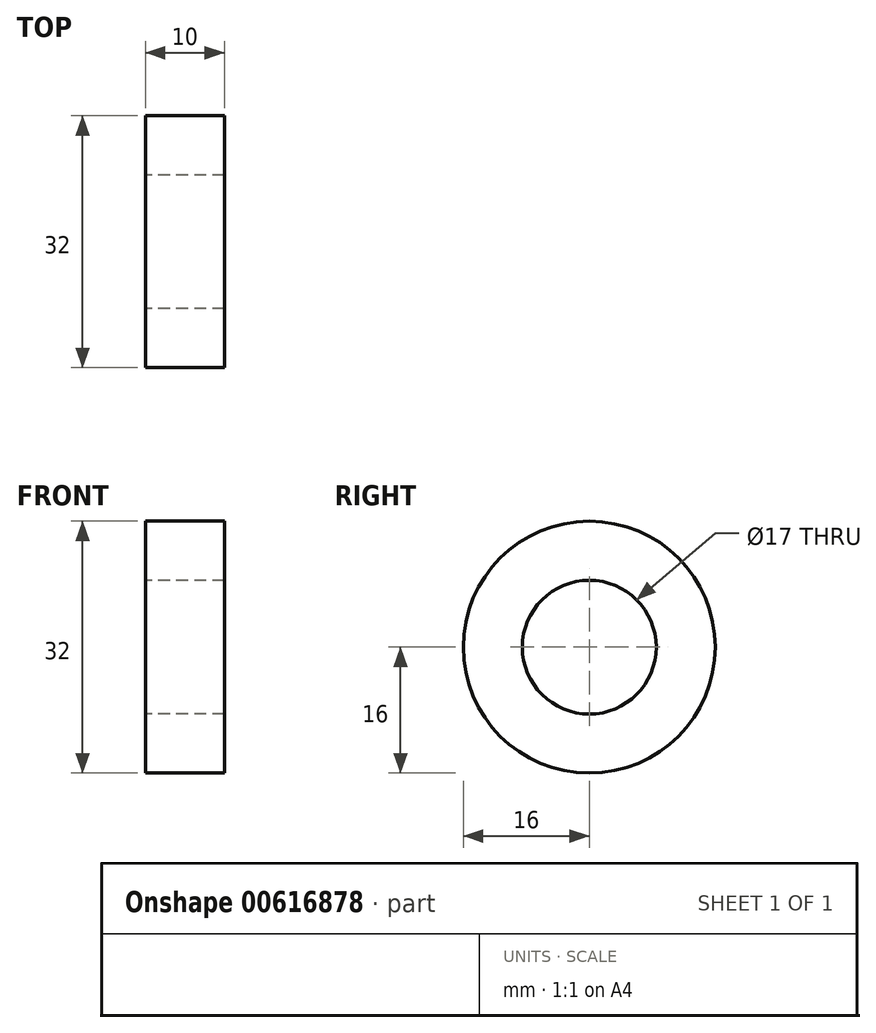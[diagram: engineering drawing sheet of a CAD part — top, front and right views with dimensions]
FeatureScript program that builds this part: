
annotation { "Feature Type Name" : "Feature", "Feature Type Description" : "" }
export const myFeature = defineFeature(function(context is Context, id is Id, definition is map)
    precondition{}
    {
        {
            var Q0;
            Q0=qCreatedBy(makeId("Right.planeOp"),FACE);
            var sketch = newSketch(context, id + "F0", { "sketchPlane" : qUnion([Q0])});
            skCircle(sketch, "E0", {"center": v(0, 0) * mm, "radius": 8.5 * mm});
            skCircle(sketch, "E1", {"center": v(0, 0) * mm, "radius": 16 * mm});
            skSolve(sketch);
        }
        {
            var Q0;
            Q0=makeQuery(id+"F0.imprint","IMPRINT",FACE,{"disambiguationData":[TD([[makeQuery(id+"F0.imprint","IMPRINT",EDGE,{"derivedFrom":sQuery(id+"F0.wireOp",EDGE,"E0")}),-1.0]])]});
            extrude(context, id + "F1", {"entities" : qUnion([Q0]), "depth" : 10 * mm, "offsetDistance" : 25 * mm});
        }
    });
